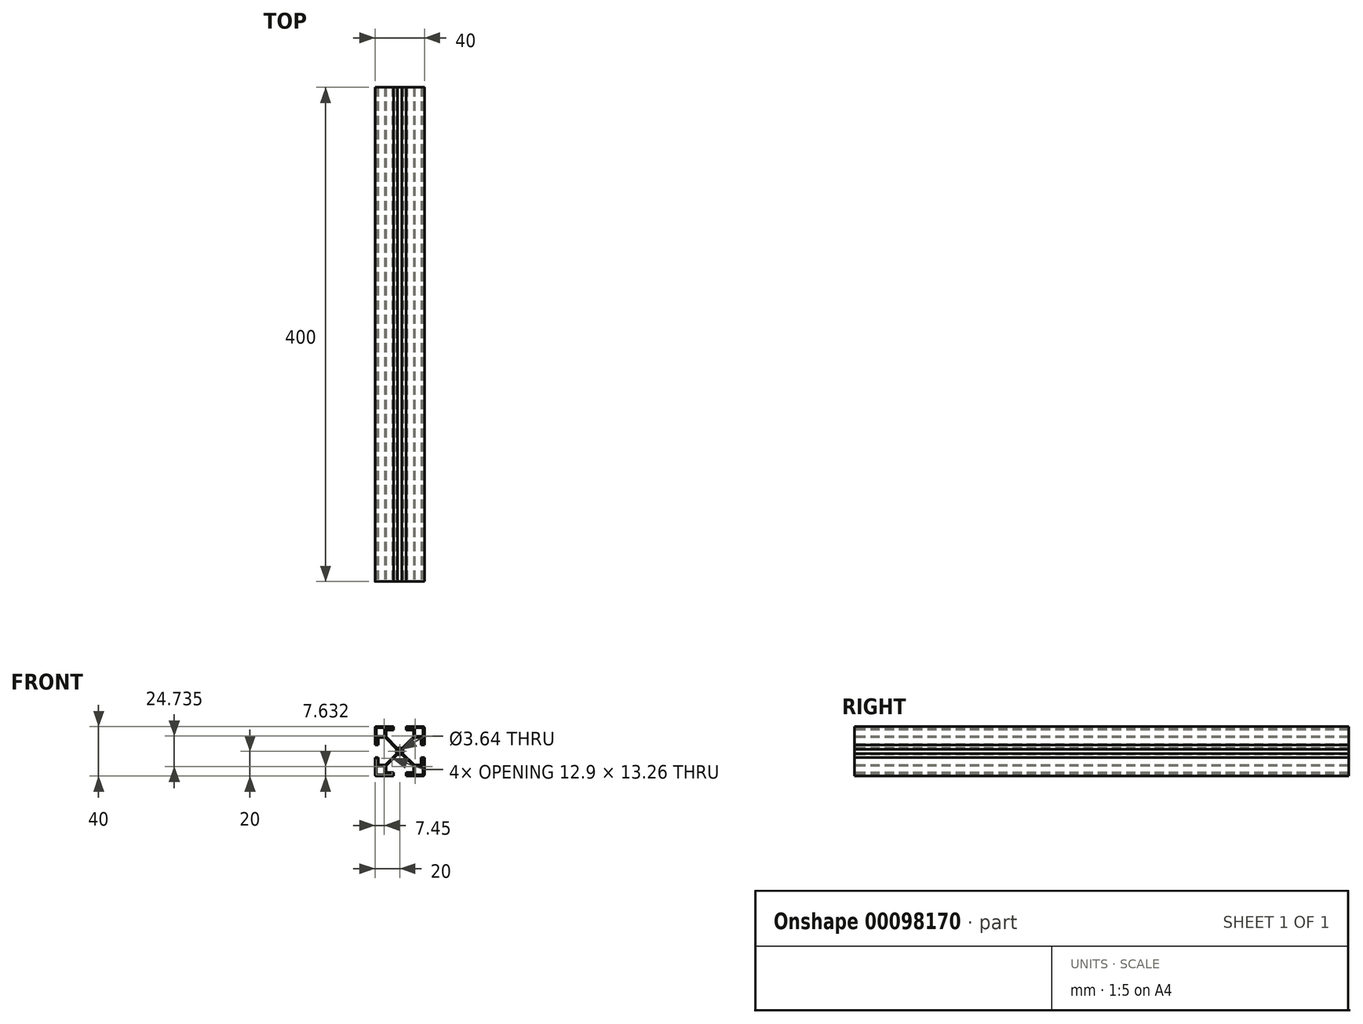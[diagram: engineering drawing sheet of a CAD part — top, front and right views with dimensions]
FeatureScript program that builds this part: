
annotation { "Feature Type Name" : "Feature", "Feature Type Description" : "" }
export const myFeature = defineFeature(function(context is Context, id is Id, definition is map)
    precondition{}
    {
        {
            var Q0;
            Q0=qCreatedBy(makeId("Front.planeOp"),FACE);
            var sketch = newSketch(context, id + "F0", { "sketchPlane" : qUnion([Q0])});
            skLineSegment(sketch, "E0", {"start": v(-60.76, 63.46) * mm, "end": v(-46.86, 63.46) * mm});
            skLineSegment(sketch, "E1", {"start": v(-61.76, 62.46) * mm, "end": v(-61.76, 48.56) * mm});
            skLineSegment(sketch, "E2", {"start": v(-41.76, 62.45) * mm, "end": v(-41.76, 5.18) * mm, "construction": true});
            skLineSegment(sketch, "E3", {"start": v(-69.79, 43.46) * mm, "end": v(51.08, 43.46) * mm, "construction": true});
            skLineSegment(sketch, "E4", {"start": v(-46.86, 63.46) * mm, "end": v(-46.86, 60.7) * mm});
            skLineSegment(sketch, "E5", {"start": v(-61.76, 48.56) * mm, "end": v(-59.01, 48.56) * mm});
            skLineSegment(sketch, "E6", {"start": v(-46.86, 60.7) * mm, "end": v(-52.86, 60.7) * mm});
            skLineSegment(sketch, "E7", {"start": v(-59.01, 48.56) * mm, "end": v(-59.01, 54.56) * mm});
            skLineSegment(sketch, "E8", {"start": v(-59.01, 54.56) * mm, "end": v(-53.51, 54.56) * mm});
            skLineSegment(sketch, "E9", {"start": v(-52.86, 60.7) * mm, "end": v(-52.86, 55.2) * mm});
            skLineSegment(sketch, "E10", {"start": v(-53.51, 54.56) * mm, "end": v(-44.12, 45.17) * mm});
            skLineSegment(sketch, "E11", {"start": v(-52.86, 55.2) * mm, "end": v(-43.47, 45.82) * mm});
            skLineSegment(sketch, "E12.MirrorCS", {"start": v(-36.66, 63.46) * mm, "end": v(-36.66, 60.7) * mm});
            skLineSegment(sketch, "E13.MirrorCS", {"start": v(-24.51, 54.56) * mm, "end": v(-30.01, 54.56) * mm});
            skLineSegment(sketch, "E14.MirrorCS", {"start": v(-21.76, 62.46) * mm, "end": v(-21.76, 48.56) * mm});
            skLineSegment(sketch, "E15.MirrorCS", {"start": v(-22.76, 63.46) * mm, "end": v(-36.66, 63.46) * mm});
            skLineSegment(sketch, "E16.MirrorCS", {"start": v(-30.01, 54.56) * mm, "end": v(-39.4, 45.17) * mm});
            skLineSegment(sketch, "E17.MirrorCS", {"start": v(-21.76, 48.56) * mm, "end": v(-24.51, 48.56) * mm});
            skLineSegment(sketch, "E18.MirrorCS", {"start": v(-24.51, 48.56) * mm, "end": v(-24.51, 54.56) * mm});
            skLineSegment(sketch, "E19.MirrorCS", {"start": v(-36.66, 60.7) * mm, "end": v(-30.66, 60.7) * mm});
            skLineSegment(sketch, "E20.MirrorCS", {"start": v(-30.66, 55.2) * mm, "end": v(-40.05, 45.82) * mm});
            skLineSegment(sketch, "E21.MirrorCS", {"start": v(-30.66, 60.7) * mm, "end": v(-30.66, 55.2) * mm});
            skLineSegment(sketch, "E22.MirrorCS", {"start": v(-22.76, 23.46) * mm, "end": v(-36.66, 23.46) * mm});
            skLineSegment(sketch, "E23.MirrorCS", {"start": v(-60.76, 23.46) * mm, "end": v(-46.86, 23.46) * mm});
            skLineSegment(sketch, "E24.MirrorCS", {"start": v(-30.66, 31.7) * mm, "end": v(-40.05, 41.1) * mm});
            skLineSegment(sketch, "E25.MirrorCS", {"start": v(-36.66, 26.2) * mm, "end": v(-30.66, 26.2) * mm});
            skLineSegment(sketch, "E26.MirrorCS", {"start": v(-36.66, 23.46) * mm, "end": v(-36.66, 26.2) * mm});
            skLineSegment(sketch, "E27.MirrorCS", {"start": v(-59.01, 32.36) * mm, "end": v(-53.51, 32.36) * mm});
            skLineSegment(sketch, "E28.MirrorCS", {"start": v(-59.01, 38.36) * mm, "end": v(-59.01, 32.36) * mm});
            skLineSegment(sketch, "E29.MirrorCS", {"start": v(-46.86, 26.2) * mm, "end": v(-52.86, 26.2) * mm});
            skLineSegment(sketch, "E30.MirrorCS", {"start": v(-21.76, 24.46) * mm, "end": v(-21.76, 38.36) * mm});
            skLineSegment(sketch, "E31.MirrorCS", {"start": v(-30.01, 32.36) * mm, "end": v(-39.4, 41.75) * mm});
            skLineSegment(sketch, "E32.MirrorCS", {"start": v(-24.51, 38.36) * mm, "end": v(-24.51, 32.36) * mm});
            skLineSegment(sketch, "E33.MirrorCS", {"start": v(-52.86, 26.2) * mm, "end": v(-52.86, 31.7) * mm});
            skLineSegment(sketch, "E34.MirrorCS", {"start": v(-46.86, 23.46) * mm, "end": v(-46.86, 26.2) * mm});
            skLineSegment(sketch, "E35.MirrorCS", {"start": v(-21.76, 38.36) * mm, "end": v(-24.51, 38.36) * mm});
            skLineSegment(sketch, "E36.MirrorCS", {"start": v(-53.51, 32.36) * mm, "end": v(-44.12, 41.75) * mm});
            skLineSegment(sketch, "E37.MirrorCS", {"start": v(-30.66, 26.2) * mm, "end": v(-30.66, 31.7) * mm});
            skLineSegment(sketch, "E38.MirrorCS", {"start": v(-52.86, 31.7) * mm, "end": v(-43.47, 41.1) * mm});
            skLineSegment(sketch, "E39.MirrorCS", {"start": v(-61.76, 38.36) * mm, "end": v(-59.01, 38.36) * mm});
            skLineSegment(sketch, "E40.MirrorCS", {"start": v(-61.76, 24.46) * mm, "end": v(-61.76, 38.36) * mm});
            skLineSegment(sketch, "E41.MirrorCS", {"start": v(-24.51, 32.36) * mm, "end": v(-30.01, 32.36) * mm});
            skArc(sketch, "E42", {"start": v(-43.47, 41.1) * mm, "mid": v(-41.76, 40.54) * mm, "end": v(-40.05, 41.1) * mm});
            skPoint(sketch, "E43.orphan", {"position": v(-41.76, 44.1) * mm});
            skPoint(sketch, "E44.orphan", {"position": v(-41.11, 43.46) * mm});
            skPoint(sketch, "E45.orphan", {"position": v(-41.76, 42.8) * mm});
            skPoint(sketch, "E46.orphan", {"position": v(-42.41, 43.46) * mm});
            skArc(sketch, "E47.trimOffspring", {"start": v(-44.12, 45.17) * mm, "mid": v(-44.68, 43.46) * mm, "end": v(-44.12, 41.75) * mm});
            skArc(sketch, "E48.trimOffspring", {"start": v(-40.05, 45.82) * mm, "mid": v(-41.76, 46.38) * mm, "end": v(-43.47, 45.82) * mm});
            skArc(sketch, "E49.trimOffspring", {"start": v(-39.4, 41.75) * mm, "mid": v(-38.84, 43.46) * mm, "end": v(-39.4, 45.17) * mm});
            skLineSegment(sketch, "E50", {"start": v(-60.76, 62.46) * mm, "end": v(-60.76, 55.56) * mm});
            skLineSegment(sketch, "E51", {"start": v(-60.01, 55.56) * mm, "end": v(-53.86, 55.56) * mm});
            skLineSegment(sketch, "E52", {"start": v(-53.86, 55.56) * mm, "end": v(-53.86, 61.7) * mm});
            skLineSegment(sketch, "E53", {"start": v(-53.86, 62.46) * mm, "end": v(-60.76, 62.46) * mm});
            skLineSegment(sketch, "E54", {"start": v(-60.76, 55.56) * mm, "end": v(-60.76, 49.2) * mm});
            skLineSegment(sketch, "E55", {"start": v(-60.76, 49.2) * mm, "end": v(-60.01, 49.2) * mm});
            skLineSegment(sketch, "E56", {"start": v(-60.01, 49.2) * mm, "end": v(-60.01, 55.56) * mm});
            skLineSegment(sketch, "E57", {"start": v(-53.86, 62.46) * mm, "end": v(-47.86, 62.46) * mm});
            skLineSegment(sketch, "E58", {"start": v(-47.86, 62.46) * mm, "end": v(-47.86, 61.7) * mm});
            skLineSegment(sketch, "E59", {"start": v(-47.86, 61.7) * mm, "end": v(-53.86, 61.7) * mm});
            skLineSegment(sketch, "E60.MirrorCS", {"start": v(-22.76, 62.46) * mm, "end": v(-22.76, 55.56) * mm});
            skLineSegment(sketch, "E61.MirrorCS", {"start": v(-22.76, 55.56) * mm, "end": v(-22.76, 49.2) * mm});
            skLineSegment(sketch, "E62.MirrorCS", {"start": v(-22.76, 49.2) * mm, "end": v(-23.51, 49.2) * mm});
            skLineSegment(sketch, "E63.MirrorCS", {"start": v(-23.51, 49.2) * mm, "end": v(-23.51, 55.56) * mm});
            skLineSegment(sketch, "E64.MirrorCS", {"start": v(-23.51, 55.56) * mm, "end": v(-29.66, 55.56) * mm});
            skLineSegment(sketch, "E65.MirrorCS", {"start": v(-29.66, 55.56) * mm, "end": v(-29.66, 61.7) * mm});
            skLineSegment(sketch, "E66.MirrorCS", {"start": v(-35.66, 61.7) * mm, "end": v(-29.66, 61.7) * mm});
            skLineSegment(sketch, "E67.MirrorCS", {"start": v(-35.66, 62.46) * mm, "end": v(-35.66, 61.7) * mm});
            skLineSegment(sketch, "E68.MirrorCS", {"start": v(-29.66, 62.46) * mm, "end": v(-22.76, 62.46) * mm});
            skLineSegment(sketch, "E69.MirrorCS", {"start": v(-29.66, 62.46) * mm, "end": v(-35.66, 62.46) * mm});
            skLineSegment(sketch, "E70.MirrorCS", {"start": v(-35.66, 24.46) * mm, "end": v(-35.66, 25.2) * mm});
            skLineSegment(sketch, "E71.MirrorCS", {"start": v(-22.76, 37.72) * mm, "end": v(-23.51, 37.72) * mm});
            skLineSegment(sketch, "E72.MirrorCS", {"start": v(-22.76, 31.36) * mm, "end": v(-22.76, 37.72) * mm});
            skLineSegment(sketch, "E73.MirrorCS", {"start": v(-23.51, 37.72) * mm, "end": v(-23.51, 31.36) * mm});
            skLineSegment(sketch, "E74.MirrorCS", {"start": v(-23.51, 31.36) * mm, "end": v(-29.66, 31.36) * mm});
            skLineSegment(sketch, "E75.MirrorCS", {"start": v(-22.76, 24.46) * mm, "end": v(-22.76, 31.36) * mm});
            skLineSegment(sketch, "E76.MirrorCS", {"start": v(-29.66, 31.36) * mm, "end": v(-29.66, 25.2) * mm});
            skLineSegment(sketch, "E77.MirrorCS", {"start": v(-35.66, 25.2) * mm, "end": v(-29.66, 25.2) * mm});
            skLineSegment(sketch, "E78.MirrorCS", {"start": v(-29.66, 24.46) * mm, "end": v(-35.66, 24.46) * mm});
            skLineSegment(sketch, "E79.MirrorCS", {"start": v(-29.66, 24.46) * mm, "end": v(-22.76, 24.46) * mm});
            skLineSegment(sketch, "E80.MirrorCS", {"start": v(-60.01, 37.72) * mm, "end": v(-60.01, 31.36) * mm});
            skLineSegment(sketch, "E81.MirrorCS", {"start": v(-60.76, 31.36) * mm, "end": v(-60.76, 37.72) * mm});
            skLineSegment(sketch, "E82.MirrorCS", {"start": v(-60.76, 37.72) * mm, "end": v(-60.01, 37.72) * mm});
            skLineSegment(sketch, "E83.MirrorCS", {"start": v(-60.01, 31.36) * mm, "end": v(-53.86, 31.36) * mm});
            skLineSegment(sketch, "E84.MirrorCS", {"start": v(-53.86, 31.36) * mm, "end": v(-53.86, 25.2) * mm});
            skLineSegment(sketch, "E85.MirrorCS", {"start": v(-47.86, 25.2) * mm, "end": v(-53.86, 25.2) * mm});
            skLineSegment(sketch, "E86.MirrorCS", {"start": v(-47.86, 24.46) * mm, "end": v(-47.86, 25.2) * mm});
            skLineSegment(sketch, "E87.MirrorCS", {"start": v(-53.86, 24.46) * mm, "end": v(-47.86, 24.46) * mm});
            skLineSegment(sketch, "E88.MirrorCS", {"start": v(-60.76, 24.46) * mm, "end": v(-60.76, 31.36) * mm});
            skLineSegment(sketch, "E89.MirrorCS", {"start": v(-53.86, 24.46) * mm, "end": v(-60.76, 24.46) * mm});
            skPoint(sketch, "E90.visualSharp", {"position": v(-61.76, 63.46) * mm});
            skArc(sketch, "E90.filletArc", {"start": v(-60.76, 63.46) * mm, "mid": v(-61.47, 63.17) * mm, "end": v(-61.76, 62.46) * mm});
            skPoint(sketch, "E91.visualSharp", {"position": v(-21.76, 63.46) * mm});
            skArc(sketch, "E91.filletArc", {"start": v(-21.76, 62.46) * mm, "mid": v(-22.05, 63.17) * mm, "end": v(-22.76, 63.46) * mm});
            skPoint(sketch, "E92.visualSharp", {"position": v(-21.76, 23.46) * mm});
            skArc(sketch, "E92.filletArc", {"start": v(-22.76, 23.46) * mm, "mid": v(-22.05, 23.75) * mm, "end": v(-21.76, 24.46) * mm});
            skPoint(sketch, "E93.visualSharp", {"position": v(-61.76, 23.46) * mm});
            skArc(sketch, "E93.filletArc", {"start": v(-61.76, 24.46) * mm, "mid": v(-61.47, 23.75) * mm, "end": v(-60.76, 23.46) * mm});
            skCircle(sketch, "E94", {"center": v(-41.76, 43.46) * mm, "radius": 1.82 * mm});
            skSolve(sketch);
        }
        {
            var Q0;
            Q0=makeQuery(id+"F0.imprint","IMPRINT",FACE,{"disambiguationData":[TD([[makeQuery(id+"F0.imprint","IMPRINT",EDGE,{"derivedFrom":sQuery(id+"F0.wireOp",EDGE,"E0")}),-1.0]])]});
            extrude(context, id + "F1", {"entities" : qUnion([Q0]), "oppositeDirection" : true, "depth" : 400 * mm});
        }
    });
